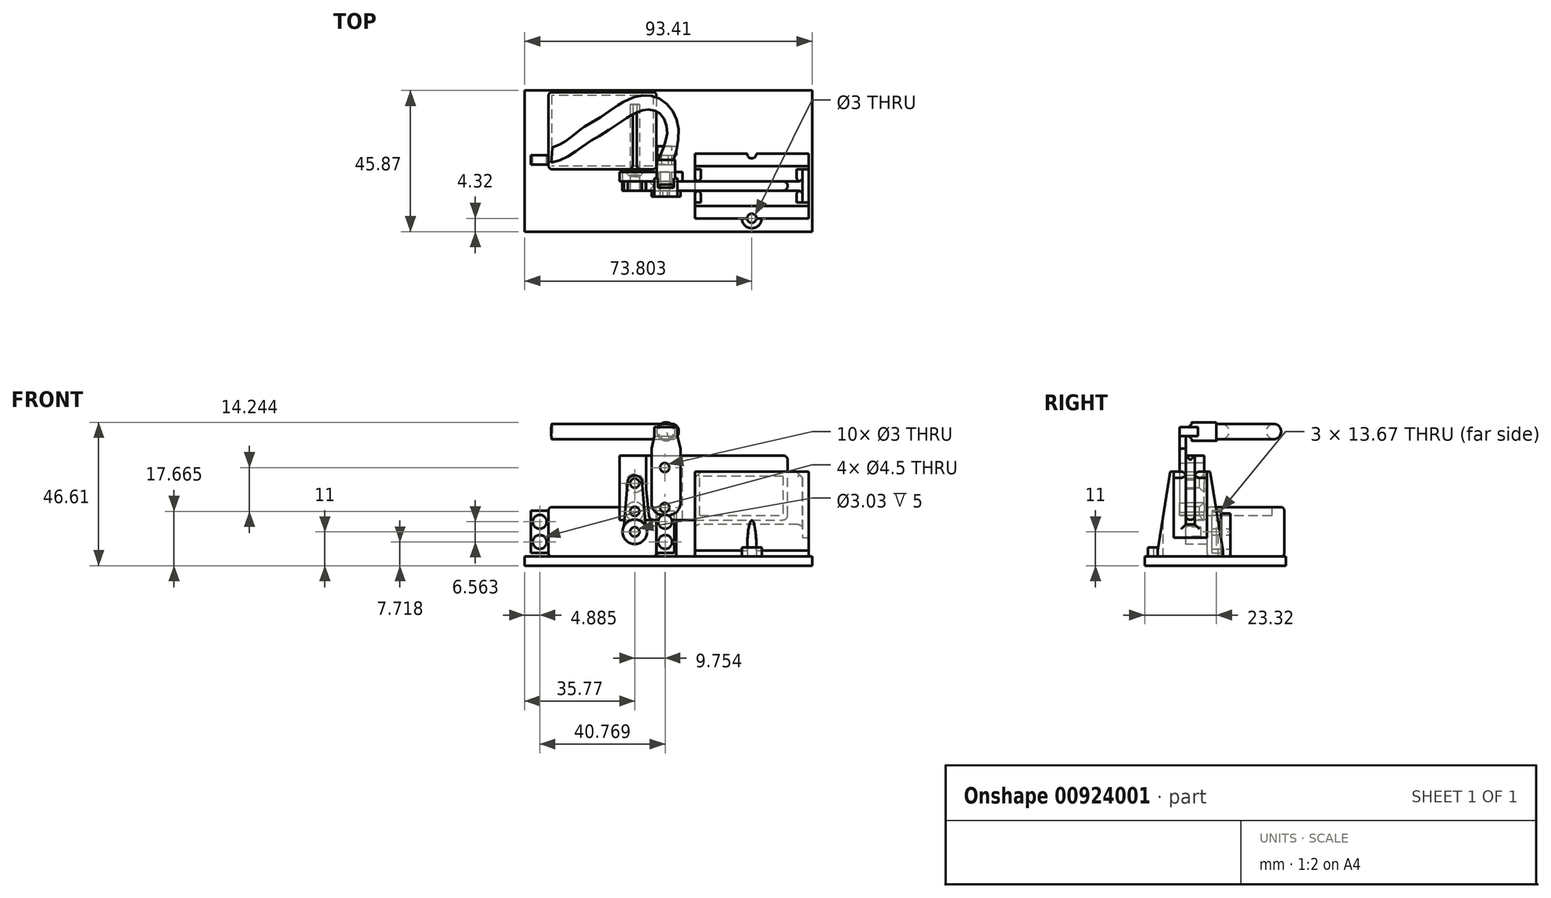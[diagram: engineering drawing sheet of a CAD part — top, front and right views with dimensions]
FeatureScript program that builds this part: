
annotation { "Feature Type Name" : "Feature", "Feature Type Description" : "" }
export const myFeature = defineFeature(function(context is Context, id is Id, definition is map)
    precondition{}
    {
        {
            var Q0;
            Q0=qCreatedBy(makeId("Front.planeOp"),FACE);
            var sketch = newSketch(context, id + "F0", { "sketchPlane" : qUnion([Q0])});
            skLineSegment(sketch, "E0", {"start": v(2.28, 16.82) * mm, "end": v(3.58, 1.78) * mm});
            skCircle(sketch, "E1", {"center": v(0, 0) * mm, "radius": 4 * mm});
            skArc(sketch, "E2", {"start": v(2.42, 15.2) * mm, "mid": v(0, 18.3) * mm, "end": v(-2.42, 15.2) * mm});
            skLineSegment(sketch, "E3.MirrorCS", {"start": v(-2.28, 16.82) * mm, "end": v(-3.58, 1.78) * mm});
            skCircle(sketch, "E4", {"center": v(0, 15.8) * mm, "radius": 1.5 * mm});
            skCircle(sketch, "E5", {"center": v(0, 6.66) * mm, "radius": 1.5 * mm});
            skSolve(sketch);
        }
        {
            var Q0;
            {var subQ0=sQuery(id+"F0.wireOp",EDGE,"E1");var subQ1=makeQuery(id+"F0.imprint","INTERSECT",VERTEX,{"derivedFrom":[sQuery(id+"F0.wireOp",EDGE,"E0"),subQ0]});Q0=makeQuery(id+"F0.imprint","IMPRINT",FACE,{"disambiguationData":[TD([[makeQuery(id+"F0.imprint","IMPRINT",EDGE,{"disambiguationData":[TD([[subQ1,-1.0]])],"derivedFrom":subQ0}),1.0]])]});}
            extrude(context, id + "F1", {"entities" : qUnion([Q0]), "oppositeDirection" : true, "depth" : 7 * mm, "offsetDistance" : 25 * mm});
        }
        {
            var Q0;
            Q0=makeQuery(id+"F1.opExtrude","CAP_FACE",FACE,{"disambiguationData":[OSD([sQuery(id+"F0.wireOp",EDGE,"E1")])],"isStart":true});
            var sketch = newSketch(context, id + "F2", { "sketchPlane" : qUnion([Q0])});
            skCircle(sketch, "E6", {"center": v(0, 0) * mm, "radius": 1.52 * mm});
            skSolve(sketch);
        }
        {
            var Q0;
            Q0=qSketchRegion(id+"F2",true);
            extrude(context, id + "F3", {"entities" : qUnion([Q0]), "operationType" : NewBodyOperationType.REMOVE, "oppositeDirection" : true, "depth" : 5 * mm, "offsetDistance" : 25 * mm});
        }
        {
            var Q0;
            {var subQ1=sQuery(id+"F0.wireOp",EDGE,"E0");var subQ5=sQuery(id+"F0.wireOp",EDGE,"E2");var subQ7=makeQuery(id+"F0.imprint","INTERSECT",VERTEX,{"disambiguationData":[OD(0.0)],"derivedFrom":[subQ1,subQ5]});Q0=makeQuery(id+"F0.imprint","IMPRINT",FACE,{"disambiguationData":[TD([[makeQuery(id+"F0.imprint","IMPRINT",EDGE,{"disambiguationData":[TD([[subQ7,-1.0]])],"derivedFrom":subQ1}),-1.0]])]});}
            extrude(context, id + "F4", {"entities" : qUnion([Q0]), "oppositeDirection" : true, "depth" : 3 * mm, "offsetDistance" : 25 * mm});
        }
        {
            var Q0;
            Q0=makeQuery(id+"F1.opExtrude","CAP_FACE",FACE,{"disambiguationData":[OSD([sQuery(id+"F0.wireOp",EDGE,"E1")])],"isStart":false});
            var sketch = newSketch(context, id + "F5", { "sketchPlane" : qUnion([Q0])});
            skLineSegment(sketch, "E7.bottom", {"start": v(28, -8) * mm, "end": v(-7, -8) * mm});
            skLineSegment(sketch, "E7.top", {"start": v(28, 8) * mm, "end": v(-7, 8) * mm});
            skLineSegment(sketch, "E7.left", {"start": v(28, -8) * mm, "end": v(28, 8) * mm});
            skLineSegment(sketch, "E7.right", {"start": v(-7, -8) * mm, "end": v(-7, 8) * mm});
            skPoint(sketch, "E7.middle", {"position": v(10.5, 0) * mm});
            skSolve(sketch);
        }
        {
            var Q0;
            Q0=qSketchRegion(id+"F5",true);
            extrude(context, id + "F6", {"entities" : qUnion([Q0]), "depth" : 25 * mm, "offsetDistance" : 25 * mm});
        }
        {
            var Q0;
            Q0=makeQuery(id+"F4.opExtrude","CAP_FACE",FACE,{"disambiguationData":[OSD([sQuery(id+"F0.wireOp",EDGE,"E0"),sQuery(id+"F0.wireOp",EDGE,"E1"),sQuery(id+"F0.wireOp",EDGE,"E2"),sQuery(id+"F0.wireOp",EDGE,"E3.MirrorCS"),sQuery(id+"F0.wireOp",EDGE,"E4"),sQuery(id+"F0.wireOp",EDGE,"E5")])],"isStart":false});
            var sketch = newSketch(context, id + "F7", { "sketchPlane" : qUnion([Q0])});
            skLineSegment(sketch, "E8.bottom", {"start": v(4.96, 3.88) * mm, "end": v(-15.53, 3.88) * mm});
            skLineSegment(sketch, "E8.top", {"start": v(4.96, 24.85) * mm, "end": v(-15.53, 24.85) * mm});
            skLineSegment(sketch, "E8.left", {"start": v(4.96, 3.88) * mm, "end": v(4.96, 24.85) * mm});
            skLineSegment(sketch, "E8.right", {"start": v(-15.53, 3.88) * mm, "end": v(-15.53, 24.85) * mm});
            skSolve(sketch);
        }
        {
            var Q0;
            Q0=makeQuery(id+"F6.opExtrude","SWEPT_FACE",FACE,{"disambiguationData":[OSD([sQuery(id+"F5.wireOp",EDGE,"E7.left")])]});
            var Q1;
            Q1=makeQuery(id+"F6.opExtrude","SWEPT_FACE",FACE,{"disambiguationData":[OSD([sQuery(id+"F5.wireOp",EDGE,"E7.top")])]});
            var Q2;
            Q2=makeQuery(id+"F6.opExtrude","CAP_FACE",FACE,{"disambiguationData":[OSD([sQuery(id+"F5.wireOp",EDGE,"E7.bottom"),sQuery(id+"F5.wireOp",EDGE,"E7.top"),sQuery(id+"F5.wireOp",EDGE,"E7.left"),sQuery(id+"F5.wireOp",EDGE,"E7.right")])],"isStart":true});
            var Q3;
            Q3=makeQuery(id+"F6.opExtrude","CAP_FACE",FACE,{"disambiguationData":[OSD([sQuery(id+"F5.wireOp",EDGE,"E7.bottom"),sQuery(id+"F5.wireOp",EDGE,"E7.top"),sQuery(id+"F5.wireOp",EDGE,"E7.left"),sQuery(id+"F5.wireOp",EDGE,"E7.right")])],"isStart":false});
            var Q4;
            Q4=makeQuery(id+"F6.opExtrude","SWEPT_FACE",FACE,{"disambiguationData":[OSD([sQuery(id+"F5.wireOp",EDGE,"E7.bottom")])]});
            fillet(context, id + "F8", {"entities" : qUnion([Q0, Q1, Q2, Q3, Q4]), "radius" : 1 * mm, "tangentPropagation" : true, "allowEdgeOverflow" : false});
        }
        {
            var Q0;
            Q0=makeQuery(id+"F6.opExtrude","CAP_FACE",FACE,{"disambiguationData":[OSD([sQuery(id+"F5.wireOp",EDGE,"E7.bottom"),sQuery(id+"F5.wireOp",EDGE,"E7.top"),sQuery(id+"F5.wireOp",EDGE,"E7.left"),sQuery(id+"F5.wireOp",EDGE,"E7.right")])],"isStart":true});
            cPlane(context, id + "F9", {"entities" : qUnion([Q0]), "cplaneType" : CPlaneType.OFFSET, "offset" : 3 * mm, "oppositeDirection" : true, "width" : 150 * mm, "height" : 150 * mm});
        }
        {
            var Q0;
            Q0=qCreatedBy(id+"F9.planeOp",FACE);
            var sketch = newSketch(context, id + "F10", { "sketchPlane" : qUnion([Q0])});
            skLineSegment(sketch, "E9.bottom", {"start": v(-28, -6.83) * mm, "end": v(-33.8, -6.83) * mm});
            skLineSegment(sketch, "E9.top", {"start": v(-28, 6.83) * mm, "end": v(-33.8, 6.83) * mm});
            skLineSegment(sketch, "E9.left", {"start": v(-28, -6.83) * mm, "end": v(-28, 6.83) * mm});
            skLineSegment(sketch, "E9.right", {"start": v(-33.8, -6.83) * mm, "end": v(-33.8, 6.83) * mm});
            skPoint(sketch, "E9.middle", {"position": v(-30.9, 0) * mm});
            skCircle(sketch, "E10", {"center": v(-30.88, 3.28) * mm, "radius": 2.25 * mm});
            skCircle(sketch, "E11.MirrorC", {"center": v(-30.88, -3.28) * mm, "radius": 2.25 * mm});
            skSolve(sketch);
        }
        {
            var Q0;
            {var subQ5=sQuery(id+"F10.wireOp",EDGE,"E9.bottom");Q0=makeQuery(id+"F10.imprint","IMPRINT",FACE,{"disambiguationData":[TD([[makeQuery(id+"F10.imprint","IMPRINT",EDGE,{"derivedFrom":subQ5}),-1.0]])]});}
            extrude(context, id + "F11", {"entities" : qUnion([Q0]), "operationType" : NewBodyOperationType.ADD, "endBound" : BoundingType.SYMMETRIC, "depth" : 3 * mm, "offsetDistance" : 25 * mm});
        }
        {
            var Q0;
            Q0=makeQuery(id+"F6.opExtrude","SWEPT_FACE",FACE,{"disambiguationData":[OSD([sQuery(id+"F5.wireOp",EDGE,"E7.left")])]});
            var Q1;
            Q1=makeQuery(id+"F6.opExtrude","SWEPT_FACE",FACE,{"disambiguationData":[OSD([sQuery(id+"F5.wireOp",EDGE,"E7.right")])]});
            cPlane(context, id + "F12", {"entities" : qUnion([Q0, Q1]), "cplaneType" : CPlaneType.MID_PLANE, "offset" : 25 * mm, "width" : 150 * mm, "height" : 150 * mm});
        }
        {
            var Q0;
            Q0=makeQuery(id+"F6.opExtrude","SWEPT_BODY",BODY,{"disambiguationData":[OSD([sQuery(id+"F5.wireOp",EDGE,"E7.bottom"),sQuery(id+"F5.wireOp",EDGE,"E7.top"),sQuery(id+"F5.wireOp",EDGE,"E7.left"),sQuery(id+"F5.wireOp",EDGE,"E7.right")])]});
            var Q1;
            Q1=qCreatedBy(id+"F12.planeOp",FACE);
            mirror(context, id + "F13", {"entities" : qUnion([Q0]), "mirrorPlane" : qUnion([Q1])});
        }
        {
            var Q0;
            Q0=qSketchRegion(id+"F7",true);
            extrude(context, id + "F14", {"entities" : qUnion([Q0]), "depth" : 3 * mm, "offsetDistance" : 25 * mm});
        }
        {
            var Q0;
            {var subQ1=sQuery(id+"F7.wireOp",EDGE,"E8.right");var subQ3=sQuery(id+"F0.wireOp",EDGE,"E0");var subQ4=sQuery(id+"F7.wireOp",EDGE,"E8.top");var subQ5=sQuery(id+"F7.wireOp",EDGE,"E8.bottom");var subQ6=sQuery(id+"F7.wireOp",EDGE,"E8.left");Q0=makeQuery(id+"F14.boolean.opBoolean","SPLIT",FACE,{"disambiguationData":[TD([makeQuery(id+"F4.opExtrude","SWEPT_FACE",FACE,{"disambiguationData":[OSD([subQ3])]})])],"derivedFrom":makeQuery(id+"F14.opExtrude","CAP_FACE",FACE,{"disambiguationData":[OSD([subQ5,subQ4,subQ6,subQ1])],"isStart":true})});}
            var sketch = newSketch(context, id + "F15", { "sketchPlane" : qUnion([Q0])});
            skLineSegment(sketch, "E12.bottom", {"start": v(3.76, 24.85) * mm, "end": v(49.69, 24.85) * mm});
            skLineSegment(sketch, "E12.top", {"start": v(3.76, 3.88) * mm, "end": v(49.69, 3.88) * mm});
            skLineSegment(sketch, "E12.left", {"start": v(3.76, 24.85) * mm, "end": v(3.76, 3.88) * mm});
            skLineSegment(sketch, "E12.right", {"start": v(49.69, 24.85) * mm, "end": v(49.69, 3.88) * mm});
            skSolve(sketch);
        }
        {
            var Q0;
            Q0=qSketchRegion(id+"F15",true);
            extrude(context, id + "F16", {"entities" : qUnion([Q0]), "depth" : 3 * mm, "offsetDistance" : 25 * mm});
        }
        {
            var Q0;
            Q0=makeQuery(id+"F16.opExtrude","CAP_FACE",FACE,{"disambiguationData":[OSD([sQuery(id+"F15.wireOp",EDGE,"E12.bottom"),sQuery(id+"F15.wireOp",EDGE,"E12.top"),sQuery(id+"F15.wireOp",EDGE,"E12.left"),sQuery(id+"F15.wireOp",EDGE,"E12.right")])],"isStart":false});
            var sketch = newSketch(context, id + "F17", { "sketchPlane" : qUnion([Q0])});
            skCircle(sketch, "E13", {"center": v(9.75, 20.9) * mm, "radius": 1.5 * mm});
            skCircle(sketch, "E14", {"center": v(9.75, 7.9) * mm, "radius": 1.5 * mm});
            skLineSegment(sketch, "E15", {"start": v(9.75, 20.9) * mm, "end": v(9.75, 7.9) * mm, "construction": true});
            skSolve(sketch);
        }
        {
            var Q0;
            Q0=qSketchRegion(id+"F17",true);
            extrude(context, id + "F18", {"entities" : qUnion([Q0]), "operationType" : NewBodyOperationType.REMOVE, "oppositeDirection" : true, "depth" : 25 * mm, "offsetDistance" : 25 * mm});
        }
        {
            var Q0;
            Q0=makeQuery(id+"F14.opExtrude","CAP_FACE",FACE,{"disambiguationData":[OSD([sQuery(id+"F7.wireOp",EDGE,"E8.bottom"),sQuery(id+"F7.wireOp",EDGE,"E8.top"),sQuery(id+"F7.wireOp",EDGE,"E8.left"),sQuery(id+"F7.wireOp",EDGE,"E8.right")])],"isStart":true});
            var sketch = newSketch(context, id + "F19", { "sketchPlane" : qUnion([Q0])});
            skCircle(sketch, "E16.0", {"center": v(9.75, 20.9) * mm, "radius": 1.5 * mm});
            skCircle(sketch, "E17.0", {"center": v(9.75, 7.9) * mm, "radius": 1.5 * mm});
            skCircle(sketch, "E18.0", {"center": v(0, 6.66) * mm, "radius": 1.5 * mm});
            skCircle(sketch, "E19.0", {"center": v(0, 15.8) * mm, "radius": 1.5 * mm});
            skSolve(sketch);
        }
        {
            var Q0;
            Q0=qSketchRegion(id+"F19",true);
            extrude(context, id + "F20", {"entities" : qUnion([Q0]), "operationType" : NewBodyOperationType.REMOVE, "oppositeDirection" : true, "depth" : 25 * mm, "offsetDistance" : 25 * mm});
        }
        {
            var Q0;
            Q0=makeQuery(id+"F20.boolean.opBoolean","INTERSECT",EDGE,{"derivedFrom":[makeQuery(id+"F14.opExtrude","CAP_FACE",FACE,{"disambiguationData":[OSD([sQuery(id+"F7.wireOp",EDGE,"E8.bottom"),sQuery(id+"F7.wireOp",EDGE,"E8.top"),sQuery(id+"F7.wireOp",EDGE,"E8.left"),sQuery(id+"F7.wireOp",EDGE,"E8.right")])],"isStart":false}),makeQuery(id+"F20.opExtrude","SWEPT_FACE",FACE,{"disambiguationData":[OSD([sQuery(id+"F19.wireOp",EDGE,"E18.0")])]})]});
            var Q1;
            Q1=makeQuery(id+"F20.boolean.opBoolean","INTERSECT",EDGE,{"derivedFrom":[makeQuery(id+"F14.opExtrude","CAP_FACE",FACE,{"disambiguationData":[OSD([sQuery(id+"F7.wireOp",EDGE,"E8.bottom"),sQuery(id+"F7.wireOp",EDGE,"E8.top"),sQuery(id+"F7.wireOp",EDGE,"E8.left"),sQuery(id+"F7.wireOp",EDGE,"E8.right")])],"isStart":false}),makeQuery(id+"F20.opExtrude","SWEPT_FACE",FACE,{"disambiguationData":[OSD([sQuery(id+"F19.wireOp",EDGE,"E17.0")])]})]});
            var Q2;
            Q2=makeQuery(id+"F20.boolean.opBoolean","INTERSECT",EDGE,{"derivedFrom":[makeQuery(id+"F14.opExtrude","CAP_FACE",FACE,{"disambiguationData":[OSD([sQuery(id+"F7.wireOp",EDGE,"E8.bottom"),sQuery(id+"F7.wireOp",EDGE,"E8.top"),sQuery(id+"F7.wireOp",EDGE,"E8.left"),sQuery(id+"F7.wireOp",EDGE,"E8.right")])],"isStart":false}),makeQuery(id+"F20.opExtrude","SWEPT_FACE",FACE,{"disambiguationData":[OSD([sQuery(id+"F19.wireOp",EDGE,"E19.0")])]})]});
            var Q3;
            Q3=makeQuery(id+"F20.boolean.opBoolean","INTERSECT",EDGE,{"derivedFrom":[makeQuery(id+"F14.opExtrude","CAP_FACE",FACE,{"disambiguationData":[OSD([sQuery(id+"F7.wireOp",EDGE,"E8.bottom"),sQuery(id+"F7.wireOp",EDGE,"E8.top"),sQuery(id+"F7.wireOp",EDGE,"E8.left"),sQuery(id+"F7.wireOp",EDGE,"E8.right")])],"isStart":false}),makeQuery(id+"F20.opExtrude","SWEPT_FACE",FACE,{"disambiguationData":[OSD([sQuery(id+"F19.wireOp",EDGE,"E16.0")])]})]});
            chamfer(context, id + "F21", {"entities" : qUnion([Q0, Q1, Q2, Q3]), "width" : 1.5 * mm, "tangentPropagation" : true});
        }
        {
            var Q0;
            Q0=makeQuery(id+"F16.opExtrude","SWEPT_EDGE",EDGE,{"disambiguationData":[OSD([sQuery(id+"F7.wireOp",EDGE,"E8.bottom"),sQuery(id+"F15.wireOp",EDGE,"E12.top"),sQuery(id+"F15.wireOp",EDGE,"E12.left")])]});
            chamfer(context, id + "F22", {"entities" : qUnion([Q0]), "chamferType" : ChamferType.TWO_OFFSETS, "width1" : 1 * mm, "oppositeDirection" : false, "width2" : 10 * mm, "tangentPropagation" : true});
        }
        {
            var Q0;
            Q0=makeQuery(id+"F16.opExtrude","SWEPT_FACE",FACE,{"disambiguationData":[OSD([sQuery(id+"F15.wireOp",EDGE,"E12.top")])]});
            var Q1;
            Q1=makeQuery(id+"F16.opExtrude","SWEPT_FACE",FACE,{"disambiguationData":[OSD([sQuery(id+"F15.wireOp",EDGE,"E12.right")])]});
            fillet(context, id + "F23", {"entities" : qUnion([Q0, Q1]), "radius" : 1.5 * mm, "tangentPropagation" : true, "allowEdgeOverflow" : false});
        }
        {
            var Q0;
            Q0=makeQuery(id+"F16.opExtrude","CAP_FACE",FACE,{"disambiguationData":[OSD([sQuery(id+"F15.wireOp",EDGE,"E12.bottom"),sQuery(id+"F15.wireOp",EDGE,"E12.top"),sQuery(id+"F15.wireOp",EDGE,"E12.left"),sQuery(id+"F15.wireOp",EDGE,"E12.right")])],"isStart":false});
            var sketch = newSketch(context, id + "F24", { "sketchPlane" : qUnion([Q0])});
            skLineSegment(sketch, "E20.bottom", {"start": v(5.43, 31.1) * mm, "end": v(14.85, 31.1) * mm});
            skLineSegment(sketch, "E20.top", {"start": v(5.43, 5.38) * mm, "end": v(14.85, 5.38) * mm});
            skLineSegment(sketch, "E20.left", {"start": v(5.43, 31.1) * mm, "end": v(5.43, 5.38) * mm});
            skLineSegment(sketch, "E20.right", {"start": v(14.85, 31.1) * mm, "end": v(14.85, 5.38) * mm});
            skCircle(sketch, "E21.0", {"center": v(9.75, 20.9) * mm, "radius": 1.5 * mm});
            skCircle(sketch, "E21.1", {"center": v(9.75, 7.9) * mm, "radius": 1.5 * mm});
            skSolve(sketch);
        }
        {
            var Q0;
            Q0=qSketchRegion(id+"F24",true);
            extrude(context, id + "F25", {"entities" : qUnion([Q0]), "depth" : 2 * mm, "offsetDistance" : 25 * mm});
        }
        {
            var Q0;
            Q0=makeQuery(id+"F25.opExtrude","SWEPT_EDGE",EDGE,{"disambiguationData":[OSD([sQuery(id+"F15.wireOp",EDGE,"E12.bottom"),sQuery(id+"F15.wireOp",EDGE,"E12.top"),sQuery(id+"F15.wireOp",EDGE,"E12.left"),sQuery(id+"F15.wireOp",EDGE,"E12.right"),sQuery(id+"F24.wireOp",EDGE,"E20.top"),sQuery(id+"F24.wireOp",EDGE,"E20.right")])]});
            var Q1;
            Q1=makeQuery(id+"F25.opExtrude","SWEPT_EDGE",EDGE,{"disambiguationData":[OSD([sQuery(id+"F15.wireOp",EDGE,"E12.bottom"),sQuery(id+"F15.wireOp",EDGE,"E12.top"),sQuery(id+"F15.wireOp",EDGE,"E12.left"),sQuery(id+"F15.wireOp",EDGE,"E12.right"),sQuery(id+"F24.wireOp",EDGE,"E20.top"),sQuery(id+"F24.wireOp",EDGE,"E20.left")])]});
            fillet(context, id + "F26", {"entities" : qUnion([Q0, Q1]), "radius" : 4 * mm, "tangentPropagation" : true, "allowEdgeOverflow" : false});
        }
        {
            var Q0;
            Q0=makeQuery(id+"F25.opExtrude","SWEPT_EDGE",EDGE,{"disambiguationData":[OSD([sQuery(id+"F24.wireOp",EDGE,"E20.bottom"),sQuery(id+"F24.wireOp",EDGE,"E20.right")])]});
            var Q1;
            Q1=makeQuery(id+"F25.opExtrude","SWEPT_EDGE",EDGE,{"disambiguationData":[OSD([sQuery(id+"F24.wireOp",EDGE,"E20.bottom"),sQuery(id+"F24.wireOp",EDGE,"E20.left")])]});
            chamfer(context, id + "F27", {"entities" : qUnion([Q0, Q1]), "chamferType" : ChamferType.TWO_OFFSETS, "width1" : 1 * mm, "oppositeDirection" : false, "width2" : 4 * mm, "tangentPropagation" : true});
        }
        {
            var Q0;
            Q0=makeQuery(id+"F25.opExtrude","CAP_FACE",FACE,{"disambiguationData":[OSD([sQuery(id+"F24.wireOp",EDGE,"E20.bottom"),sQuery(id+"F24.wireOp",EDGE,"E20.top"),sQuery(id+"F24.wireOp",EDGE,"E20.left"),sQuery(id+"F24.wireOp",EDGE,"E20.right"),sQuery(id+"F24.wireOp",EDGE,"E21.0"),sQuery(id+"F24.wireOp",EDGE,"E21.1")])],"isStart":true});
            var sketch = newSketch(context, id + "F28", { "sketchPlane" : qUnion([Q0])});
            skLineSegment(sketch, "E22.bottom", {"start": v(-13.85, 34.1) * mm, "end": v(-6.43, 34.1) * mm});
            skLineSegment(sketch, "E22.top", {"start": v(-13.85, 31.1) * mm, "end": v(-6.43, 31.1) * mm});
            skLineSegment(sketch, "E22.left", {"start": v(-13.85, 34.1) * mm, "end": v(-13.85, 31.1) * mm});
            skLineSegment(sketch, "E22.right", {"start": v(-6.43, 34.1) * mm, "end": v(-6.43, 31.1) * mm});
            skSolve(sketch);
        }
        {
            var Q0;
            Q0=qSketchRegion(id+"F28",true);
            var Q1;
            Q1=makeQuery(id+"F25.opExtrude","CAP_FACE",FACE,{"disambiguationData":[OSD([sQuery(id+"F24.wireOp",EDGE,"E20.bottom"),sQuery(id+"F24.wireOp",EDGE,"E20.top"),sQuery(id+"F24.wireOp",EDGE,"E20.left"),sQuery(id+"F24.wireOp",EDGE,"E20.right"),sQuery(id+"F24.wireOp",EDGE,"E21.0"),sQuery(id+"F24.wireOp",EDGE,"E21.1")])],"isStart":false});
            extrude(context, id + "F29", {"entities" : qUnion([Q0]), "operationType" : NewBodyOperationType.ADD, "depth" : 4 * mm, "offsetDistance" : 25 * mm, "hasSecondDirection" : true, "secondDirectionBound" : SecondDirectionBoundingType.UP_TO_SURFACE, "secondDirectionOppositeDirection" : true, "secondDirectionDepth" : 2 * mm, "secondDirectionBoundEntityFace" : qUnion([Q1])});
        }
        {
            var Q0;
            Q0=makeQuery(id+"F29.opExtrude","CAP_FACE",FACE,{"disambiguationData":[OSD([sQuery(id+"F28.wireOp",EDGE,"E22.bottom"),sQuery(id+"F28.wireOp",EDGE,"E22.top"),sQuery(id+"F28.wireOp",EDGE,"E22.left"),sQuery(id+"F28.wireOp",EDGE,"E22.right")])],"isStart":false});
            var sketch = newSketch(context, id + "F30", { "sketchPlane" : qUnion([Q0])});
            skCircle(sketch, "E23", {"center": v(-10.14, 32.6) * mm, "radius": 3 * mm});
            skPoint(sketch, "E23.centerSnap0", {"position": v(-13.85, 32.6) * mm});
            skPoint(sketch, "E23.centerSnap1", {"position": v(-10.14, 34.1) * mm});
            skSolve(sketch);
        }
        {
            var Q0;
            Q0=qSketchRegion(id+"F30",true);
            extrude(context, id + "F31", {"entities" : qUnion([Q0]), "operationType" : NewBodyOperationType.ADD, "depth" : 6 * mm, "offsetDistance" : 25 * mm, "hasSecondDirection" : true, "secondDirectionOppositeDirection" : true, "secondDirectionDepth" : 2 * mm});
        }
        {
            var Q0;
            Q0=makeQuery(id+"F31.boolean.opBoolean","INTERSECT",EDGE,{"derivedFrom":[makeQuery(id+"F29.opExtrude","SWEPT_FACE",FACE,{"disambiguationData":[OSD([sQuery(id+"F28.wireOp",EDGE,"E22.bottom")])]}),makeQuery(id+"F31.opExtrude","CAP_FACE",FACE,{"disambiguationData":[OSD([sQuery(id+"F30.wireOp",EDGE,"E23")])],"isStart":true})]});
            var Q1;
            Q1=makeQuery(id+"F31.boolean.opBoolean","INTERSECT",EDGE,{"derivedFrom":[makeQuery(id+"F29.opExtrude","SWEPT_FACE",FACE,{"disambiguationData":[OSD([sQuery(id+"F28.wireOp",EDGE,"E22.top")])]}),makeQuery(id+"F31.opExtrude","CAP_FACE",FACE,{"disambiguationData":[OSD([sQuery(id+"F30.wireOp",EDGE,"E23")])],"isStart":true})]});
            chamfer(context, id + "F32", {"entities" : qUnion([Q0, Q1]), "width" : 1 * mm, "tangentPropagation" : true});
        }
        {
            var Q0;
            Q0=makeQuery(id+"F29.opExtrude","CAP_EDGE",EDGE,{"disambiguationData":[OSD([sQuery(id+"F28.wireOp",EDGE,"E22.left")])],"isStart":false});
            cPoint(context, id + "F33", {"entities" : qUnion([Q0]), "parameter" : 0.5});
        }
        {
            var Q0;
            Q0=qCreatedBy(id+"F33",VERTEX);
            var Q1;
            Q1=makeQuery(id+"F29.opExtrude","SWEPT_FACE",FACE,{"disambiguationData":[OSD([sQuery(id+"F28.wireOp",EDGE,"E22.bottom")])]});
            cPlane(context, id + "F34", {"entities" : qUnion([Q0, Q1]), "cplaneType" : CPlaneType.PLANE_POINT, "offset" : 25 * mm, "width" : 150 * mm, "height" : 150 * mm});
        }
        {
            var Q0;
            Q0=qCreatedBy(id+"F34.planeOp",FACE);
            var sketch = newSketch(context, id + "F35", { "sketchPlane" : qUnion([Q0])});
            skLineSegment(sketch, "E24", {"start": v(10.09, 10.18) * mm, "end": v(10.09, 17.23) * mm});
            skFitSpline(sketch, "E25", {"points": [v(10.09, 17.23) * mm, v(1.82, 27.1) * mm, v(-10.5, 21.79) * mm, v(-21.08, 15.65) * mm, v(-34.17, 12.09) * mm], "startDerivative": vector(-2.62, 81.29) * mm, "endDerivative": vector(-67.56, 3.13) * mm});
            skSolve(sketch);
        }
        {
            var Q0;
            Q0=makeQuery(id+"F31.opExtrude","CAP_FACE",FACE,{"disambiguationData":[OSD([sQuery(id+"F30.wireOp",EDGE,"E23")])],"isStart":false});
            var sketch = newSketch(context, id + "F36", { "sketchPlane" : qUnion([Q0])});
            skCircle(sketch, "E26", {"center": v(-10.14, 32.6) * mm, "radius": 2.5 * mm});
            skSolve(sketch);
        }
        {
            var Q0;
            Q0=makeQuery(id+"F36.imprint","IMPRINT",FACE,{"disambiguationData":[TD([[makeQuery(id+"F36.imprint","IMPRINT",EDGE,{"derivedFrom":sQuery(id+"F36.wireOp",EDGE,"E26")}),1.0]])]});
            var Q1;
            Q1=sQuery(id+"F35.wireOp",EDGE,"E25");
            sweep(context, id + "F37", {"profiles" : qUnion([Q0]), "path" : qUnion([Q1])});
        }
        {
            var Q0;
            Q0=makeQuery(id+"F14.opExtrude","SWEPT_FACE",FACE,{"disambiguationData":[OSD([sQuery(id+"F7.wireOp",EDGE,"E8.right")])]});
            cPlane(context, id + "F38", {"entities" : qUnion([Q0]), "cplaneType" : CPlaneType.OFFSET, "offset" : 4 * mm, "width" : 150 * mm, "height" : 150 * mm});
        }
        {
            var Q0;
            Q0=qCreatedBy(id+"F38.planeOp",FACE);
            var sketch = newSketch(context, id + "F39", { "sketchPlane" : qUnion([Q0])});
            skLineSegment(sketch, "E27", {"start": v(3, 19.58) * mm, "end": v(6.9, 19.58) * mm});
            skLineSegment(sketch, "E28", {"start": v(6.9, 19.58) * mm, "end": v(6.9, -1.82) * mm});
            skLineSegment(sketch, "E29", {"start": v(6.9, -1.82) * mm, "end": v(1.5, -1.82) * mm});
            skLineSegment(sketch, "E30", {"start": v(1.5, -1.82) * mm, "end": v(1.5, 2.4) * mm});
            skLineSegment(sketch, "E31", {"start": v(1.5, 2.4) * mm, "end": v(3, 2.4) * mm});
            skLineSegment(sketch, "E32", {"start": v(3, 2.4) * mm, "end": v(3, 19.58) * mm});
            skSolve(sketch);
        }
        {
            var Q0;
            Q0=qSketchRegion(id+"F39",true);
            extrude(context, id + "F40", {"entities" : qUnion([Q0]), "depth" : 35 * mm, "offsetDistance" : 25 * mm});
        }
        {
            var Q0;
            Q0=makeQuery(id+"F40.opExtrude","CAP_EDGE",EDGE,{"disambiguationData":[OSD([sQuery(id+"F39.wireOp",EDGE,"E27")])],"isStart":false});
            var Q1;
            Q1=makeQuery(id+"F40.opExtrude","CAP_EDGE",EDGE,{"disambiguationData":[OSD([sQuery(id+"F39.wireOp",EDGE,"E27")])],"isStart":true});
            chamfer(context, id + "F41", {"entities" : qUnion([Q0, Q1]), "width" : 2 * mm, "tangentPropagation" : true});
        }
        {
            var Q0;
            Q0=makeQuery(id+"F40.opExtrude","SWEPT_EDGE",EDGE,{"disambiguationData":[OSD([sQuery(id+"F39.wireOp",EDGE,"E27"),sQuery(id+"F39.wireOp",EDGE,"E32")])]});
            var Q1;
            Q1=makeQuery(id+"F40.opExtrude","CAP_EDGE",EDGE,{"disambiguationData":[OSD([sQuery(id+"F39.wireOp",EDGE,"E32")])],"isStart":false});
            var Q2;
            Q2=makeQuery(id+"F40.opExtrude","CAP_EDGE",EDGE,{"disambiguationData":[OSD([sQuery(id+"F39.wireOp",EDGE,"E31")])],"isStart":false});
            var Q3;
            Q3=makeQuery(id+"F40.opExtrude","CAP_EDGE",EDGE,{"disambiguationData":[OSD([sQuery(id+"F39.wireOp",EDGE,"E32")])],"isStart":true});
            var Q4;
            Q4=makeQuery(id+"F40.opExtrude","CAP_EDGE",EDGE,{"disambiguationData":[OSD([sQuery(id+"F39.wireOp",EDGE,"E31")])],"isStart":true});
            fillet(context, id + "F42", {"entities" : qUnion([Q0, Q1, Q2, Q3, Q4]), "radius" : 1.5 * mm, "tangentPropagation" : true, "allowEdgeOverflow" : false});
        }
        {
            var Q0;
            Q0=makeQuery(id+"F40.opExtrude","SWEPT_BODY",BODY,{"disambiguationData":[OSD([sQuery(id+"F39.wireOp",EDGE,"E27"),sQuery(id+"F39.wireOp",EDGE,"E28"),sQuery(id+"F39.wireOp",EDGE,"E29"),sQuery(id+"F39.wireOp",EDGE,"E30"),sQuery(id+"F39.wireOp",EDGE,"E31"),sQuery(id+"F39.wireOp",EDGE,"E32")])]});
            var Q1;
            Q1=makeQuery(id+"F40.opExtrude","SWEPT_FACE",FACE,{"disambiguationData":[OSD([sQuery(id+"F39.wireOp",EDGE,"E30")])]});
            mirror(context, id + "F43", {"operationType" : NewBodyOperationType.ADD, "entities" : qUnion([Q0]), "mirrorPlane" : qUnion([Q1])});
        }
        {
            var Q0;
            {var subQ0=makeQuery(id+"F40.opExtrude","CAP_FACE",FACE,{"disambiguationData":[OSD([sQuery(id+"F39.wireOp",EDGE,"E27"),sQuery(id+"F39.wireOp",EDGE,"E28"),sQuery(id+"F39.wireOp",EDGE,"E29"),sQuery(id+"F39.wireOp",EDGE,"E30"),sQuery(id+"F39.wireOp",EDGE,"E31"),sQuery(id+"F39.wireOp",EDGE,"E32")])],"isStart":false});Q0=makeQuery(id+"F43.boolean.opBoolean","MERGE",FACE,{"derivedFrom":[subQ0,makeQuery(id+"F43.opPattern","COPY",FACE,{"derivedFrom":subQ0,"instanceName":"1"})]});}
            var sketch = newSketch(context, id + "F44", { "sketchPlane" : qUnion([Q0])});
            skLineSegment(sketch, "E33", {"start": v(6.9, 19.58) * mm, "end": v(7.98, 19.58) * mm});
            skLineSegment(sketch, "E34", {"start": v(7.98, 19.58) * mm, "end": v(12.08, -6.03) * mm});
            skLineSegment(sketch, "E35", {"start": v(12.08, -6.03) * mm, "end": v(12.08, -8) * mm});
            skLineSegment(sketch, "E36", {"start": v(12.08, -8) * mm, "end": v(1.5, -8) * mm});
            skLineSegment(sketch, "E37", {"start": v(1.5, -8) * mm, "end": v(1.5, -1.82) * mm});
            skLineSegment(sketch, "E38", {"start": v(1.5, -1.82) * mm, "end": v(6.9, -1.82) * mm});
            skLineSegment(sketch, "E39", {"start": v(6.9, -1.82) * mm, "end": v(6.9, 19.58) * mm});
            skSolve(sketch);
        }
        {
            var Q0;
            {var subQ0=sQuery(id+"F44.wireOp",EDGE,"E33");Q0=makeQuery(id+"F44.imprint","IMPRINT",FACE,{"disambiguationData":[TD([[makeQuery(id+"F44.imprint","IMPRINT",EDGE,{"derivedFrom":subQ0}),-1.0]])]});}
            extrude(context, id + "F45", {"entities" : qUnion([Q0]), "oppositeDirection" : true, "depth" : 35 * mm, "offsetDistance" : 25 * mm, "hasSecondDirection" : true, "secondDirectionOppositeDirection" : false, "secondDirectionDepth" : 2 * mm});
        }
        {
            var Q0;
            Q0=makeQuery(id+"F45.opExtrude","SWEPT_BODY",BODY,{"disambiguationData":[OSD([sQuery(id+"F44.wireOp",EDGE,"YrtFYt9k-314d-4dnt-fFpS-7pII2GoBX3Ag"),sQuery(id+"F44.wireOp",EDGE,"E33"),sQuery(id+"F44.wireOp",EDGE,"E34"),sQuery(id+"F44.wireOp",EDGE,"E35"),sQuery(id+"F44.wireOp",EDGE,"E36"),sQuery(id+"F44.wireOp",EDGE,"E37"),sQuery(id+"F44.wireOp",EDGE,"E38"),sQuery(id+"F44.wireOp",EDGE,"E39")])]});
            var Q1;
            Q1=makeQuery(id+"F45.opExtrude","SWEPT_FACE",FACE,{"disambiguationData":[OSD([sQuery(id+"F44.wireOp",EDGE,"E37")])]});
            mirror(context, id + "F46", {"operationType" : NewBodyOperationType.ADD, "entities" : qUnion([Q0]), "mirrorPlane" : qUnion([Q1])});
        }
        {
            var Q0;
            {var subQ0=makeQuery(id+"F45.opExtrude","SWEPT_FACE",FACE,{"disambiguationData":[OSD([sQuery(id+"F44.wireOp",EDGE,"E36")])]});Q0=makeQuery(id+"F46.boolean.opBoolean","MERGE",FACE,{"derivedFrom":[subQ0,makeQuery(id+"F46.opPattern","COPY",FACE,{"derivedFrom":subQ0,"instanceName":"1"})]});}
            var sketch = newSketch(context, id + "F47", { "sketchPlane" : qUnion([Q0])});
            skLineSegment(sketch, "E40", {"start": v(38.03, 9.08) * mm, "end": v(38.03, -12.08) * mm, "construction": true});
            skLineSegment(sketch, "E41", {"start": v(19.53, -1.5) * mm, "end": v(56.53, -1.5) * mm, "construction": true});
            skCircle(sketch, "E42", {"center": v(38.03, 7.5) * mm, "radius": 1.5 * mm});
            skCircle(sketch, "E43.MirrorC", {"center": v(38.03, -10.5) * mm, "radius": 1.5 * mm});
            skSolve(sketch);
        }
        {
            var Q0;
            Q0=makeQuery(id+"F47.imprint","IMPRINT",FACE,{"disambiguationData":[TD([[makeQuery(id+"F47.imprint","IMPRINT",EDGE,{"derivedFrom":sQuery(id+"F47.wireOp",EDGE,"E42")}),-1.0]])]});
            var sketch = newSketch(context, id + "F48", { "sketchPlane" : qUnion([Q0])});
            skArc(sketch, "E44", {"start": v(41.25, 9.08) * mm, "mid": v(38.03, 12.22) * mm, "end": v(34.81, 9.08) * mm});
            skLineSegment(sketch, "E45", {"start": v(34.81, 9.08) * mm, "end": v(41.25, 9.08) * mm});
            skArc(sketch, "E46.MirrorCS", {"start": v(41.25, -12.08) * mm, "mid": v(38.03, -15.22) * mm, "end": v(34.81, -12.08) * mm});
            skLineSegment(sketch, "E47.MirrorCS", {"start": v(34.81, -12.08) * mm, "end": v(41.25, -12.08) * mm});
            skSolve(sketch);
        }
        {
            var Q0;
            Q0=makeQuery(id+"F48.imprint","IMPRINT",FACE,{"disambiguationData":[TD([[makeQuery(id+"F48.imprint","IMPRINT",EDGE,{"derivedFrom":sQuery(id+"F48.wireOp",EDGE,"E44")}),1.0]])]});
            var Q1;
            Q1=makeQuery(id+"F48.imprint","IMPRINT",FACE,{"disambiguationData":[TD([[makeQuery(id+"F48.imprint","IMPRINT",EDGE,{"derivedFrom":sQuery(id+"F48.wireOp",EDGE,"E46.MirrorCS")}),-1.0]])]});
            extrude(context, id + "F49", {"entities" : qUnion([Q0, Q1]), "operationType" : NewBodyOperationType.ADD, "oppositeDirection" : true, "depth" : 3 * mm, "offsetDistance" : 25 * mm});
        }
        {
            var Q0;
            {var subQ0=makeQuery(id+"F45.opExtrude","SWEPT_FACE",FACE,{"disambiguationData":[OSD([sQuery(id+"F44.wireOp",EDGE,"E36")])]});Q0=makeQuery(id+"F49.boolean.opBoolean","MERGE",FACE,{"derivedFrom":[makeQuery(id+"F46.boolean.opBoolean","MERGE",FACE,{"derivedFrom":[subQ0,makeQuery(id+"F46.opPattern","COPY",FACE,{"derivedFrom":subQ0,"instanceName":"1"})]}),makeQuery(id+"F49.opExtrude","CAP_FACE",FACE,{"disambiguationData":[OSD([sQuery(id+"F48.wireOp",EDGE,"E44"),sQuery(id+"F48.wireOp",EDGE,"E45")])],"isStart":true}),makeQuery(id+"F49.opExtrude","CAP_FACE",FACE,{"disambiguationData":[OSD([sQuery(id+"F48.wireOp",EDGE,"E46.MirrorCS"),sQuery(id+"F48.wireOp",EDGE,"E47.MirrorCS")])],"isStart":true})]});}
            var sketch = newSketch(context, id + "F50", { "sketchPlane" : qUnion([Q0])});
            skCircle(sketch, "E48", {"center": v(38.03, 9) * mm, "radius": 1.5 * mm});
            skCircle(sketch, "E49.MirrorC", {"center": v(38.03, -12) * mm, "radius": 1.5 * mm});
            skSolve(sketch);
        }
        {
            var Q0;
            Q0=qSketchRegion(id+"F50",true);
            extrude(context, id + "F51", {"entities" : qUnion([Q0]), "operationType" : NewBodyOperationType.REMOVE, "endBound" : BoundingType.THROUGH_ALL, "oppositeDirection" : true, "depth" : 25 * mm, "offsetDistance" : 25 * mm});
        }
        {
            var Q0;
            Q0=makeQuery(id+"F47.imprint","IMPRINT",FACE,{"disambiguationData":[TD([[makeQuery(id+"F47.imprint","IMPRINT",EDGE,{"derivedFrom":sQuery(id+"F47.wireOp",EDGE,"E42")}),-1.0]])]});
            var sketch = newSketch(context, id + "F52", { "sketchPlane" : qUnion([Q0])});
            skLineSegment(sketch, "E50.bottom", {"start": v(-35.77, 13.32) * mm, "end": v(57.64, 13.32) * mm});
            skLineSegment(sketch, "E50.top", {"start": v(-35.77, -32.55) * mm, "end": v(57.64, -32.55) * mm});
            skLineSegment(sketch, "E50.left", {"start": v(-35.77, 13.32) * mm, "end": v(-35.77, -32.55) * mm});
            skLineSegment(sketch, "E50.right", {"start": v(57.64, 13.32) * mm, "end": v(57.64, -32.55) * mm});
            skSolve(sketch);
        }
        {
            var Q0;
            Q0=qSketchRegion(id+"F52",true);
            extrude(context, id + "F53", {"entities" : qUnion([Q0]), "depth" : 3 * mm, "offsetDistance" : 25 * mm});
        }
        {
            var Q0;
            Q0=makeQuery(id+"F53.opExtrude","CAP_FACE",FACE,{"disambiguationData":[OSD([sQuery(id+"F52.wireOp",EDGE,"E50.bottom"),sQuery(id+"F52.wireOp",EDGE,"E50.top"),sQuery(id+"F52.wireOp",EDGE,"E50.left"),sQuery(id+"F52.wireOp",EDGE,"E50.right")])],"isStart":true});
            var sketch = newSketch(context, id + "F54", { "sketchPlane" : qUnion([Q0])});
            skLineSegment(sketch, "E51.bottom", {"start": v(7.25, 14.5) * mm, "end": v(13.53, 14.5) * mm});
            skLineSegment(sketch, "E51.top", {"start": v(7.25, 11.5) * mm, "end": v(13.53, 11.5) * mm});
            skLineSegment(sketch, "E51.left", {"start": v(7.25, 14.5) * mm, "end": v(7.25, 11.5) * mm});
            skLineSegment(sketch, "E51.right", {"start": v(13.53, 14.5) * mm, "end": v(13.53, 11.5) * mm});
            skSolve(sketch);
        }
        {
            var Q0;
            Q0=qSketchRegion(id+"F54",true);
            extrude(context, id + "F55", {"entities" : qUnion([Q0]), "operationType" : NewBodyOperationType.ADD, "depth" : 14 * mm, "offsetDistance" : 25 * mm});
        }
        {
            var Q0;
            Q0=makeQuery(id+"F55.opExtrude","SWEPT_FACE",FACE,{"disambiguationData":[OSD([sQuery(id+"F54.wireOp",EDGE,"E51.bottom")])]});
            var sketch = newSketch(context, id + "F56", { "sketchPlane" : qUnion([Q0])});
            skCircle(sketch, "E52.0", {"center": v(-9.88, 3.28) * mm, "radius": 2.25 * mm});
            skCircle(sketch, "E53.0", {"center": v(-9.88, -3.28) * mm, "radius": 2.25 * mm});
            skSolve(sketch);
        }
        {
            var Q0;
            Q0=qSketchRegion(id+"F56",true);
            extrude(context, id + "F57", {"entities" : qUnion([Q0]), "operationType" : NewBodyOperationType.REMOVE, "endBound" : BoundingType.THROUGH_ALL, "oppositeDirection" : true, "depth" : 25 * mm, "offsetDistance" : 25 * mm});
        }
    });
